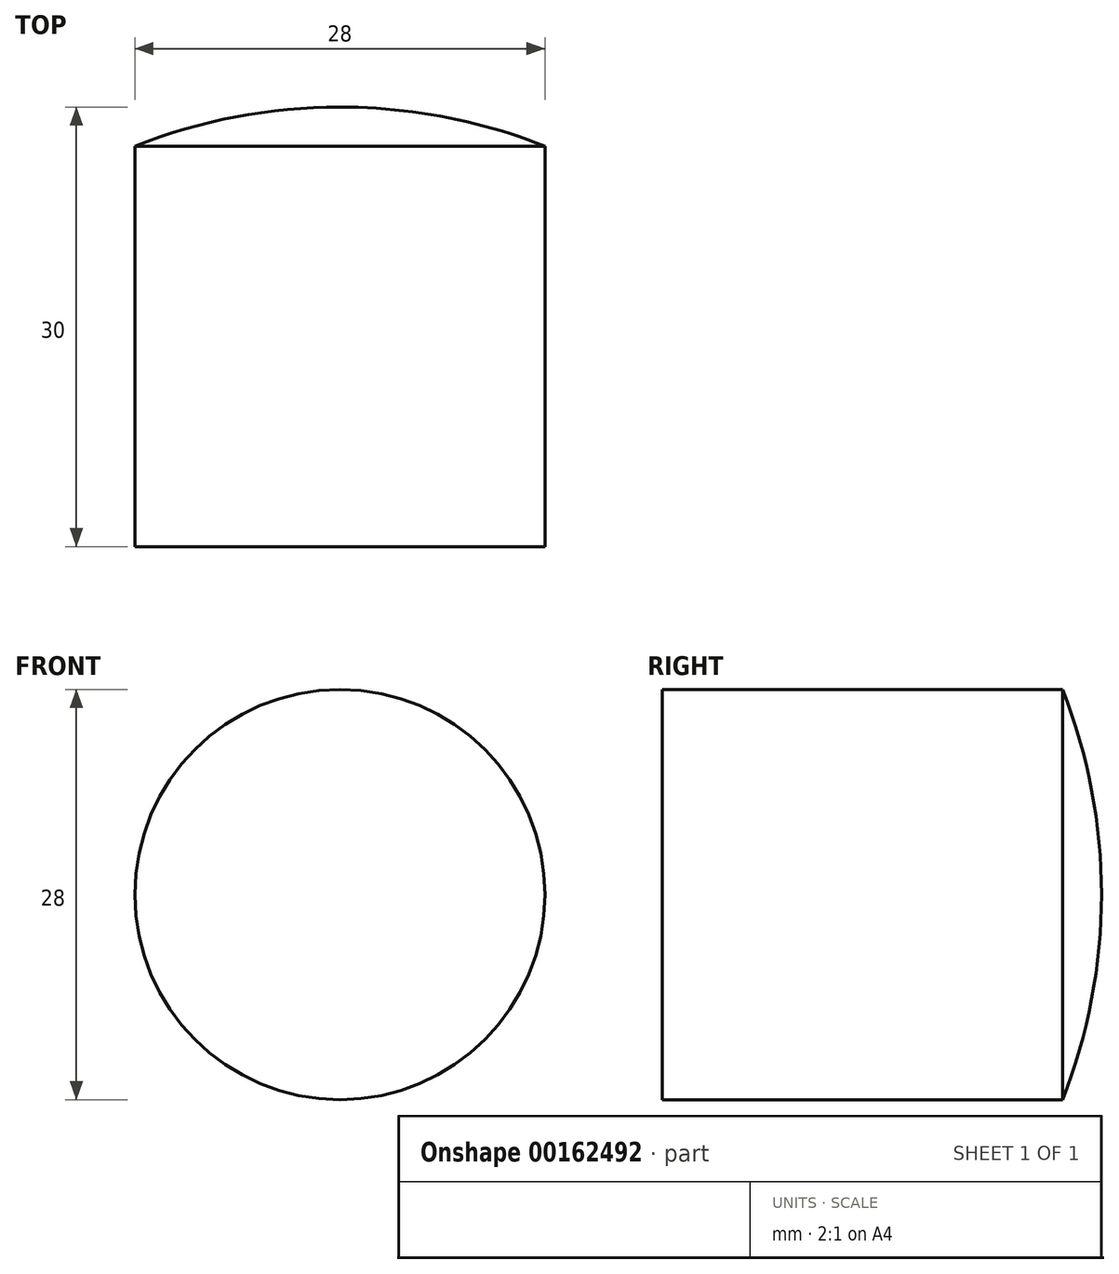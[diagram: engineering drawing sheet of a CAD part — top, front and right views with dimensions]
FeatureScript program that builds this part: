
annotation { "Feature Type Name" : "Feature", "Feature Type Description" : "" }
export const myFeature = defineFeature(function(context is Context, id is Id, definition is map)
    precondition{}
    {
        {
            var Q0;
            Q0=qCreatedBy(makeId("Top.planeOp"),FACE);
            var sketch = newSketch(context, id + "F0", { "sketchPlane" : qUnion([Q0])});
            skArc(sketch, "E0", {"start": v(0, 0) * mm, "mid": v(7.13, -0.67) * mm, "end": v(14, -2.67) * mm});
            skLineSegment(sketch, "E1", {"start": v(0, 0) * mm, "end": v(0, 22.68) * mm, "construction": true});
            skLineSegment(sketch, "E2", {"start": v(14, -2.67) * mm, "end": v(14, -30) * mm});
            skLineSegment(sketch, "E3", {"start": v(14, -30) * mm, "end": v(0, -30) * mm});
            skLineSegment(sketch, "E4", {"start": v(0, 0) * mm, "end": v(0, -30) * mm});
            skSolve(sketch);
        }
        {
            var Q0;
            Q0 = qSketchRegion(id + "F0", true);
            var Q1;
            Q1=sQuery(id+"F0.wireOp",EDGE,"E1");
            revolve(context, id + "F1", {"entities" : qUnion([Q0]), "axis" : qUnion([Q1]), "revolveType" : RevolveType.FULL});
        }
    });
